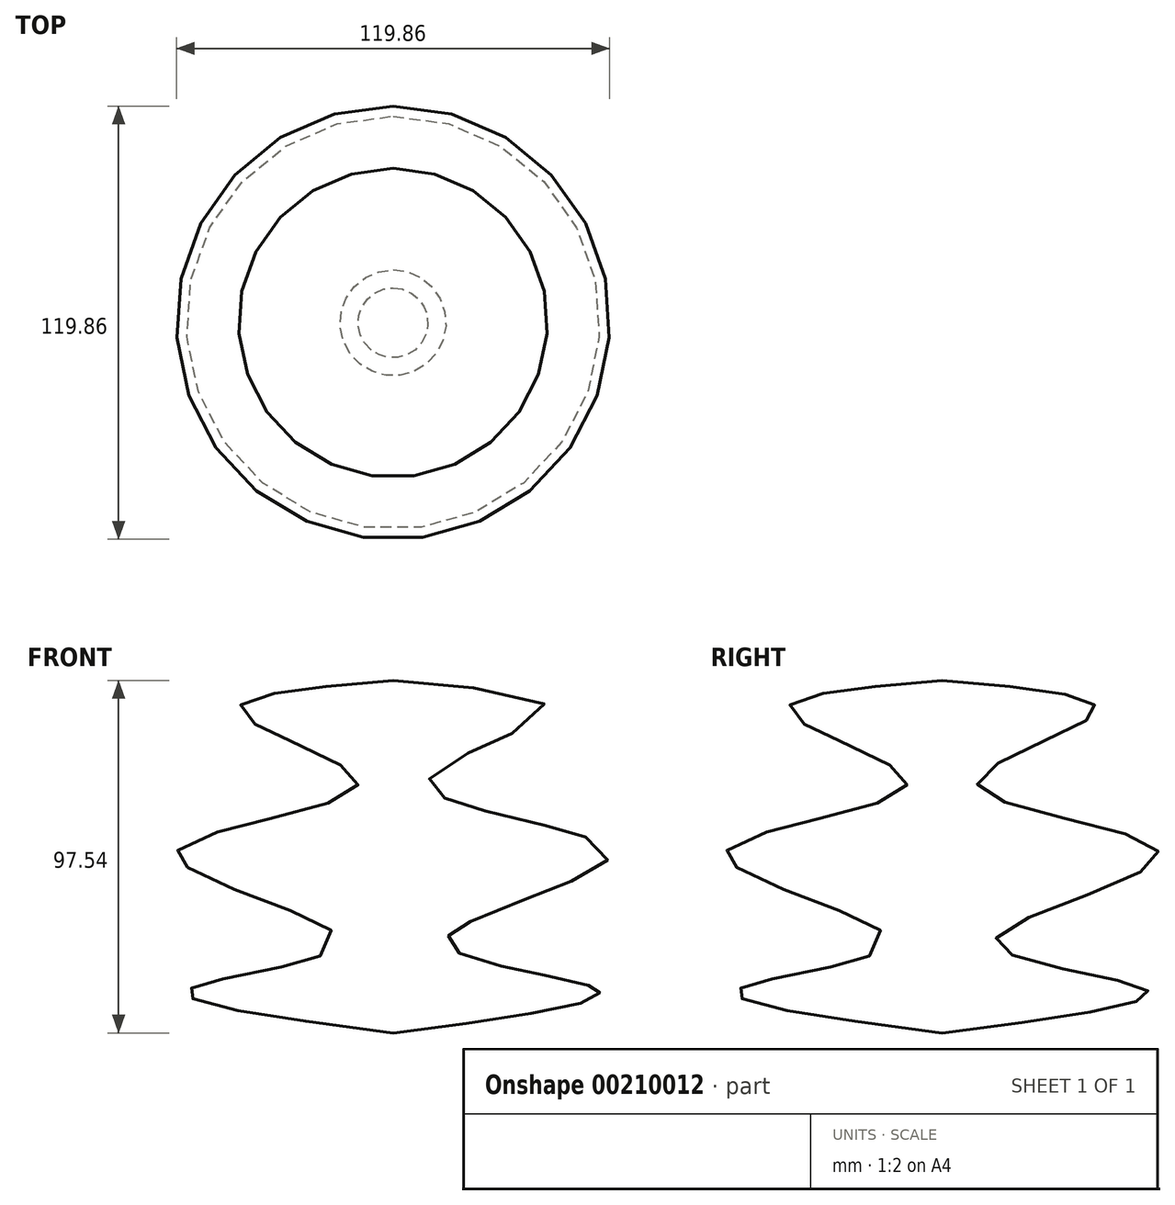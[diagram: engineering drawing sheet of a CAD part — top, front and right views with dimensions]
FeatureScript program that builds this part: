
annotation { "Feature Type Name" : "Feature", "Feature Type Description" : "" }
export const myFeature = defineFeature(function(context is Context, id is Id, definition is map)
    precondition{}
    {
        {
            var Q0;
            Q0=qCreatedBy(makeId("Right.planeOp"),FACE);
            var sketch = newSketch(context, id + "F0", { "sketchPlane" : qUnion([Q0])});
            skFitSpline(sketch, "E0", {"points": [v(0, 60.6) * mm, v(42.04, 51.13) * mm, v(9.76, 31.49) * mm, v(59.93, 12.54) * mm, v(14.67, -11.32) * mm, v(56.07, -24.65) * mm, v(0, -36.93) * mm], "startDerivative": vector(444.36, -37.25) * mm, "endDerivative": vector(-519.29, -67.15) * mm});
            skLineSegment(sketch, "E1", {"start": v(0, 69.03) * mm, "end": v(0, 88.22) * mm});
            skSolve(sketch);
        }
        {
            var Q0;
            Q0=sQuery(id+"F0.wireOp",EDGE,"E0");
            var Q1;
            Q1=sQuery(id+"F0.wireOp",EDGE,"E1");
            revolve(context, id + "F1", {"bodyType" : ToolBodyType.SURFACE, "surfaceEntities" : qUnion([Q0]), "axis" : qUnion([Q1]), "revolveType" : RevolveType.FULL});
        }
    });
